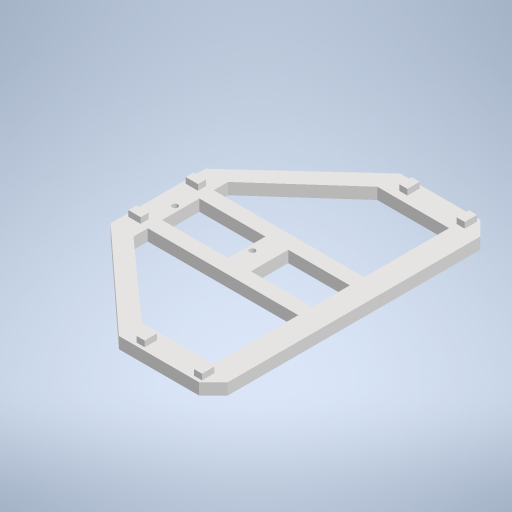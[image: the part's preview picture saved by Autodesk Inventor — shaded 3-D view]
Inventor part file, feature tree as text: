
AUTODESK INVENTOR PART (.ipt)
format: ipt  version: 2024.2 (Build 282272000, 272)  size: 352,768 bytes
history: native  units: mm
features: extrude x3, sketch x3, chamfer x1
ambient origin geometry x8: Origin, YZ Plane, XZ Plane, XY Plane, X Axis, Y Axis, Z Axis, Center Point
bodies: Solid1 (feature_tree)
feature tree (7):
  extrude  "Extrusion1"  Depth=5.0mm
  sketch  "Sketch4"  dims[d60=4.3mm d63=2.8mm]
  extrude  "Extrusion5"  Depth=2.8mm
  chamfer  "Chamfer6"  Distance=17.2mm
  extrude  "Extrusion7"  Depth=4.3mm
  sketch  "Sketch1"  dims[d18=4.0mm d19=0.0mm d57=5.0mm d58=5.0mm d59=33.0mm]
  sketch  "Sketch5"  dims[d64=2.8mm d66=17.2mm d67=4.3mm d68=1.1mm d78=2.0mm d79=0.0mm d85=33.0mm d95=8.0mm d97=98.2mm d99=59.5mm d100=8.0mm d102=68.5mm d103=8.0mm d104=13.0mm d105=23.0mm d106=13.0mm d112=8.0mm d113=8.0mm d114=8.0mm d115=8.0mm d117=42.6mm d119=8.0mm d120=13.0mm d122=8.0mm d133=5.1mm d134=1.1mm d135=5.0mm d136=2.0mm d137=45.0deg d138=5.0mm d139=5.0mm d140=37.6mm d141=5.0mm d142=2.0mm d143=2.0mm d144=2.0mm d145=2.0mm d146=6.5mm d147=6.5mm d148=9.0mm d149=0.0mm d150=4.3mm d151=2.8mm d152=4.3mm d153=2.8mm d154=17.2mm d155=1.1mm d156=5.1mm]
